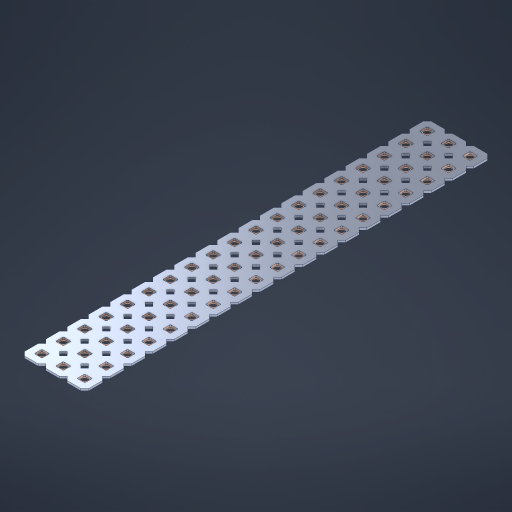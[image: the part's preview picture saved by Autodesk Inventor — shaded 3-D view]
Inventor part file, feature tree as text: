
AUTODESK INVENTOR PART (.ipt)
format: ipt  version: 2023 (Build 270158000, 158)  size: 919,552 bytes
history: native  units: in
note: dims shown in document units (in); Inventor stores cm internally (conversion verified against a paired STEP export)
features: other x58, extrude x56, sketch x2, pattern_linear x1
ambient origin geometry x8: Origin, YZ Plane, XZ Plane, XY Plane, X Axis, Y Axis, Z Axis, Center Point
bodies: Solid1 (feature_tree), Body (feature_tree)
feature tree (117):
  pattern_linear  "Rectangular Pattern1"  Spacing1=0.09in  [1 undecoded]
  sketch  "Sketch1"  dims[d1=0.5in]
  sketch  "Sketch2"  dims[d2=0.182in d3=0.09in d4=0.09in d5=0.09in d6=0.09in d7=0.09in d8=0.09in d9=0.09in d10=0.09in d11=0.02in d13=0.0in d14=0.172in d15=0.0625in d16=0.0in d19=0.5in d22=0.5in]
  other  "Srf1"
  other  "Srf126"
  other  "Srf127"
  other  "Srf128"
  other  "Srf129"
  other  "Srf130"
  other  "Srf131"
  other  "Srf250"
  other  "Srf251"
  other  "Srf252"
  other  "Srf253"
  other  "Srf254"
  other  "Srf255"
  other  "Srf256"
  other  "Srf257"
  other  "Srf258"
  other  "Srf259"
  other  "Srf260"
  other  "Srf261"
  other  "Srf268"
  other  "Srf269"
  other  "Srf270"
  other  "Srf271"
  other  "Srf272"
  other  "Srf273"
  other  "Srf274"
  other  "Srf275"
  other  "Srf276"
  other  "Srf277"
  other  "Srf278"
  other  "Srf279"
  other  "Srf280"
  other  "Srf281"
  other  "Srf282"
  other  "Srf283"
  other  "Srf284"
  other  "Srf285"
  other  "Srf286"
  other  "Srf293"
  other  "Srf294"
  other  "Srf295"
  other  "Srf296"
  other  "Srf297"
  other  "Srf298"
  other  "Srf299"
  other  "Srf300"
  other  "Srf301"
  other  "Srf302"
  other  "Srf303"
  other  "Srf304"
  other  "Srf305"
  other  "Srf306"
  other  "Srf307"
  other  "Srf308"
  other  "Srf309"
  other  "Srf310"
  other  "Srf311"
  other  "Circle"
  extrude  "ExtrusionSrf126"  Depth=0.09in
  extrude  "ExtrusionSrf127"  Depth=0.09in
  extrude  "ExtrusionSrf128"  Depth=0.09in
  extrude  "ExtrusionSrf129"  Depth=0.09in
  extrude  "ExtrusionSrf130"  Depth=0.09in
  extrude  "ExtrusionSrf131"  Depth=0.09in
  extrude  "ExtrusionSrf250"  Depth=0.09in
  extrude  "ExtrusionSrf251"  Depth=0.02in
  extrude  "ExtrusionSrf252"  TaperAngle=0.0deg  [1 undecoded]
  extrude  "ExtrusionSrf253"  Depth=0.5in
  extrude  "ExtrusionSrf254"  Depth=0.5in TaperAngle=0.0deg
  extrude  "ExtrusionSrf255"  Depth=0.5in
  extrude  "ExtrusionSrf256"  Depth=0.5in
  extrude  "ExtrusionSrf257"  [1 undecoded]
  extrude  "ExtrusionSrf258"  [1 undecoded]
  extrude  "ExtrusionSrf259"  [1 undecoded]
  extrude  "ExtrusionSrf260"  [1 undecoded]
  extrude  "ExtrusionSrf261"  [1 undecoded]
  extrude  "ExtrusionSrf268"  [1 undecoded]
  extrude  "ExtrusionSrf269"  [1 undecoded]
  extrude  "ExtrusionSrf270"  [1 undecoded]
  extrude  "ExtrusionSrf271"  [1 undecoded]
  extrude  "ExtrusionSrf272"  [1 undecoded]
  extrude  "ExtrusionSrf273"  [1 undecoded]
  extrude  "ExtrusionSrf274"  [1 undecoded]
  extrude  "ExtrusionSrf275"  [1 undecoded]
  extrude  "ExtrusionSrf276"  [1 undecoded]
  extrude  "ExtrusionSrf277"  [1 undecoded]
  extrude  "ExtrusionSrf278"  [1 undecoded]
  extrude  "ExtrusionSrf279"  [1 undecoded]
  extrude  "ExtrusionSrf280"  [1 undecoded]
  extrude  "ExtrusionSrf281"  [1 undecoded]
  extrude  "ExtrusionSrf282"  [1 undecoded]
  extrude  "ExtrusionSrf283"  [1 undecoded]
  extrude  "ExtrusionSrf284"  [1 undecoded]
  extrude  "ExtrusionSrf285"  [1 undecoded]
  extrude  "ExtrusionSrf286"  [1 undecoded]
  extrude  "ExtrusionSrf293"  [1 undecoded]
  extrude  "ExtrusionSrf294"  [1 undecoded]
  extrude  "ExtrusionSrf295"  [1 undecoded]
  extrude  "ExtrusionSrf296"  [1 undecoded]
  extrude  "ExtrusionSrf297"  [1 undecoded]
  extrude  "ExtrusionSrf298"  [1 undecoded]
  extrude  "ExtrusionSrf299"  [1 undecoded]
  extrude  "ExtrusionSrf300"  [1 undecoded]
  extrude  "ExtrusionSrf301"  [1 undecoded]
  extrude  "ExtrusionSrf302"  [1 undecoded]
  extrude  "ExtrusionSrf303"  [1 undecoded]
  extrude  "ExtrusionSrf304"  [1 undecoded]
  extrude  "ExtrusionSrf305"  [1 undecoded]
  extrude  "ExtrusionSrf306"  [1 undecoded]
  extrude  "ExtrusionSrf307"  [1 undecoded]
  extrude  "ExtrusionSrf308"  [1 undecoded]
  extrude  "ExtrusionSrf309"  [1 undecoded]
  extrude  "ExtrusionSrf310"  [1 undecoded]
  extrude  "ExtrusionSrf311"  [1 undecoded]
note: 45 required parameter values undecoded (feature->parameter linkage not recoverable at this tier; creation-order binding heuristic only, values carry confidence <= 0.55)
